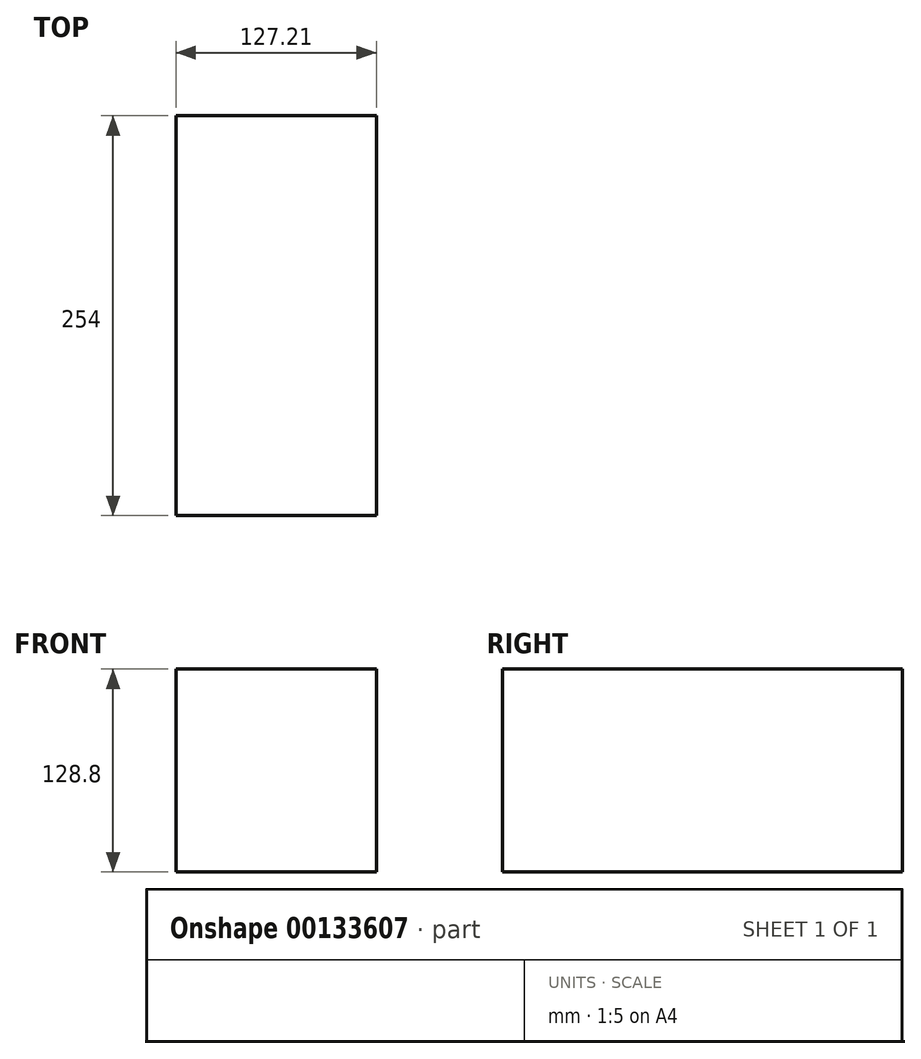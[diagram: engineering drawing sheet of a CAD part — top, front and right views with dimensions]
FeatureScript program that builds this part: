
annotation { "Feature Type Name" : "Feature", "Feature Type Description" : "" }
export const myFeature = defineFeature(function(context is Context, id is Id, definition is map)
    precondition{}
    {
        {
            var Q0;
            Q0=qCreatedBy(makeId("Front.planeOp"),FACE);
            var sketch = newSketch(context, id + "F0", { "sketchPlane" : qUnion([Q0])});
            skLineSegment(sketch, "E0.bottom", {"start": v(-42.7, 52.49) * mm, "end": v(84.5, 52.49) * mm});
            skLineSegment(sketch, "E0.top", {"start": v(-42.7, -76.3) * mm, "end": v(84.5, -76.3) * mm});
            skLineSegment(sketch, "E0.left", {"start": v(-42.7, 52.49) * mm, "end": v(-42.7, -76.3) * mm});
            skLineSegment(sketch, "E0.right", {"start": v(84.5, 52.49) * mm, "end": v(84.5, -76.3) * mm});
            skSolve(sketch);
        }
        {
            var Q0;
            Q0=makeQuery(id+"F0.imprint","IMPRINT",FACE,{"disambiguationData":[TD([[makeQuery(id+"F0.imprint","IMPRINT",EDGE,{"derivedFrom":sQuery(id+"F0.wireOp",EDGE,"E0.bottom")}),-1.0]])]});
            extrude(context, id + "F1", {"entities" : qUnion([Q0]), "depth" : 254 * mm});
        }
    });
